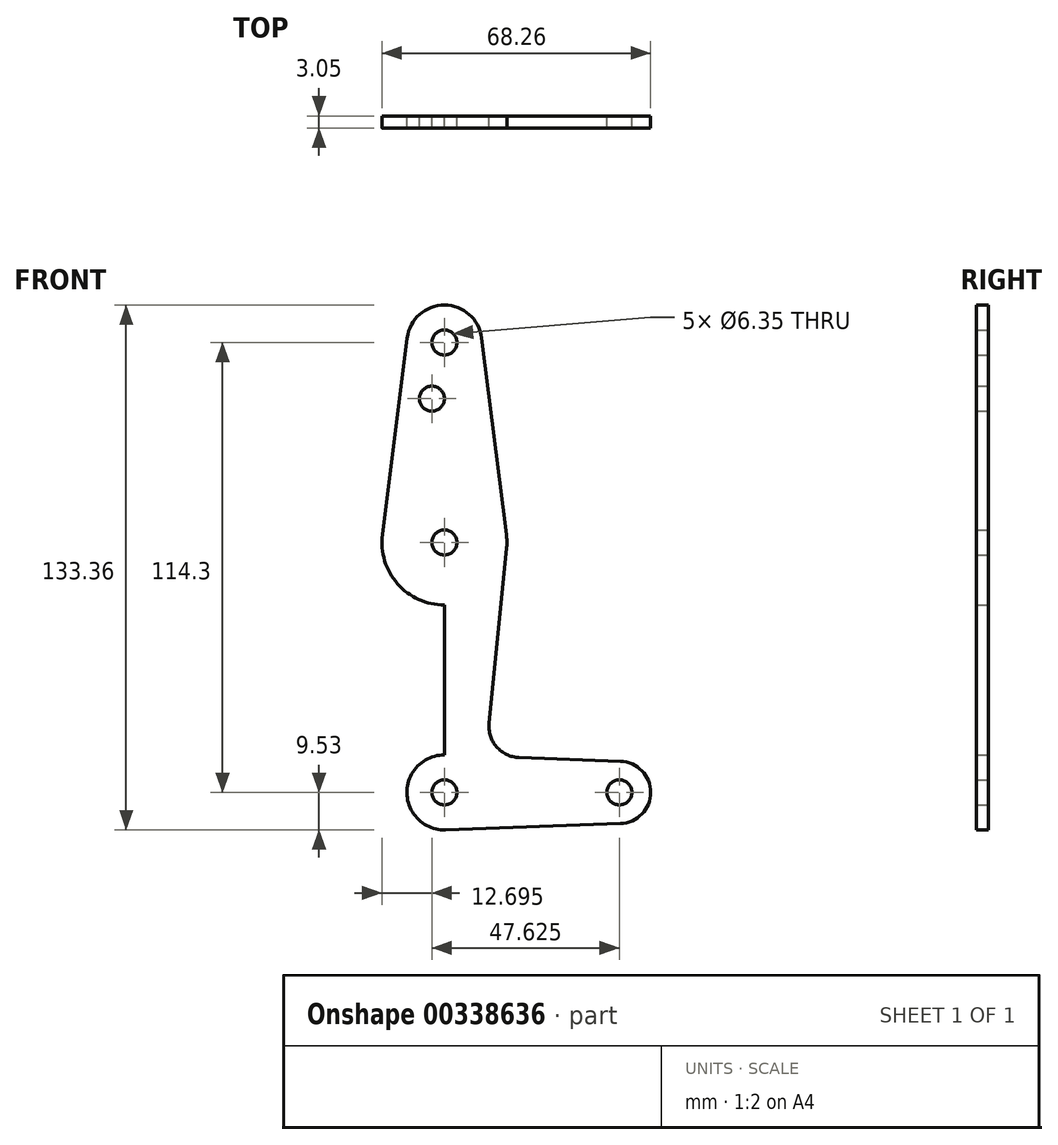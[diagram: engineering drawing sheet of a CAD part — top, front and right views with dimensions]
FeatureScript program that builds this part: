
annotation { "Feature Type Name" : "Feature", "Feature Type Description" : "" }
export const myFeature = defineFeature(function(context is Context, id is Id, definition is map)
    precondition{}
    {
        {
            var Q0;
            Q0=qCreatedBy(makeId("Front.planeOp"),FACE);
            var sketch = newSketch(context, id + "F0", { "sketchPlane" : qUnion([Q0])});
            skLineSegment(sketch, "E0", {"start": v(0, 0) * mm, "end": v(0, 123.83) * mm});
            skCircle(sketch, "E1", {"center": v(0, 0) * mm, "radius": 9.53 * mm});
            skCircle(sketch, "E2", {"center": v(44.45, 0) * mm, "radius": 7.94 * mm});
            skCircle(sketch, "E3", {"center": v(0, 63.5) * mm, "radius": 15.88 * mm});
            skCircle(sketch, "E4", {"center": v(0, 114.3) * mm, "radius": 9.53 * mm});
            skLineSegment(sketch, "E5", {"start": v(-15.75, 65.48) * mm, "end": v(-9.45, 115.5) * mm});
            skLineSegment(sketch, "E6", {"start": v(15.75, 65.48) * mm, "end": v(9.45, 115.5) * mm});
            skLineSegment(sketch, "E7", {"start": v(-15.8, 61.91) * mm, "end": v(-9.57, 0) * mm});
            skLineSegment(sketch, "E8", {"start": v(15.8, 61.91) * mm, "end": v(11.34, 17.6) * mm});
            skLineSegment(sketch, "E9", {"start": v(18.97, 8.85) * mm, "end": v(44.73, 7.93) * mm});
            skLineSegment(sketch, "E10", {"start": v(0.34, -9.52) * mm, "end": v(44.73, -7.93) * mm});
            skPoint(sketch, "E11.newPointB", {"position": v(9.57, 0) * mm});
            skArc(sketch, "E11.filletArc", {"start": v(11.34, 17.6) * mm, "mid": v(13.26, 11.57) * mm, "end": v(18.97, 8.85) * mm});
            skCircle(sketch, "E12", {"center": v(0, 114.3) * mm, "radius": 3.18 * mm});
            skCircle(sketch, "E13", {"center": v(44.45, 0) * mm, "radius": 3.18 * mm});
            skCircle(sketch, "E14", {"center": v(0, 0) * mm, "radius": 3.18 * mm});
            skCircle(sketch, "E15", {"center": v(0, 63.5) * mm, "radius": 3.18 * mm});
            skCircle(sketch, "E16", {"center": v(-3.18, 100.03) * mm, "radius": 3.18 * mm});
            skSolve(sketch);
        }
        {
            var Q0;
            Q0 = qSketchRegion(id + "F0", true);
            extrude(context, id + "F1", {"entities" : qUnion([Q0]), "depth" : 3.05 * mm});
        }
    });
